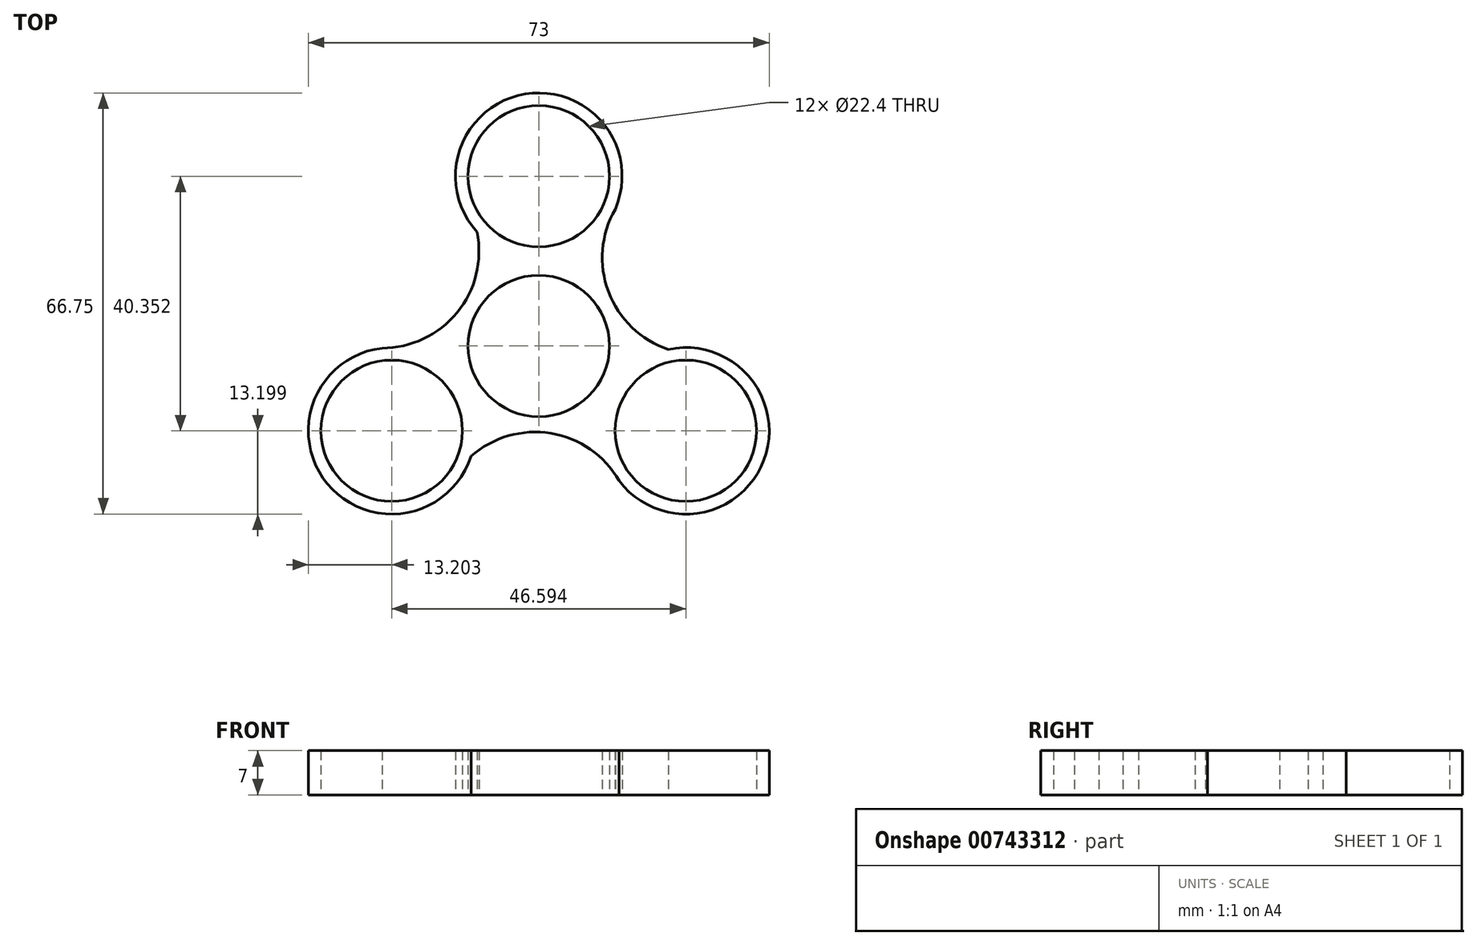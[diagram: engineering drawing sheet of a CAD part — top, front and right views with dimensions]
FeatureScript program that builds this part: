
annotation { "Feature Type Name" : "Feature", "Feature Type Description" : "" }
export const myFeature = defineFeature(function(context is Context, id is Id, definition is map)
    precondition{}
    {
        {
            var Q0;
            Q0=qCreatedBy(makeId("Top.planeOp"),FACE);
            var sketch = newSketch(context, id + "F0", { "sketchPlane" : qUnion([Q0])});
            skCircle(sketch, "E0", {"center": v(0, 0) * mm, "radius": 11.2 * mm});
            skCircle(sketch, "E1", {"center": v(0, 26.9) * mm, "radius": 11.2 * mm});
            skArc(sketch, "E2", {"start": v(11.36, 20.18) * mm, "mid": v(-1.33, 40.03) * mm, "end": v(-9.78, 18.03) * mm});
            skArc(sketch, "E3.1.0", {"start": v(-23.15, -0.25) * mm, "mid": v(-34, -21.17) * mm, "end": v(-10.73, -17.48) * mm});
            skCircle(sketch, "E3.1.1", {"center": v(-23.3, -13.45) * mm, "radius": 11.2 * mm});
            skArc(sketch, "E3.2.0", {"start": v(11.8, -19.93) * mm, "mid": v(35.34, -18.86) * mm, "end": v(20.5, -0.55) * mm});
            skCircle(sketch, "E3.2.1", {"center": v(23.3, -13.45) * mm, "radius": 11.2 * mm});
            skArc(sketch, "E4", {"start": v(12.13, 21.69) * mm, "mid": v(11.04, 8.58) * mm, "end": v(20.5, -0.55) * mm});
            skArc(sketch, "E5.1.0", {"start": v(-24.84, -0.34) * mm, "mid": v(-12.95, 5.27) * mm, "end": v(-9.78, 18.03) * mm});
            skArc(sketch, "E5.2.0", {"start": v(12.72, -21.34) * mm, "mid": v(1.91, -13.85) * mm, "end": v(-10.73, -17.48) * mm});
            skSolve(sketch);
        }
        {
            var Q0;
            Q0=makeQuery(id+"F0.imprint","IMPRINT",FACE,{"disambiguationData":[TD([[makeQuery(id+"F0.imprint","IMPRINT",EDGE,{"derivedFrom":sQuery(id+"F0.wireOp",EDGE,"E0")}),-1.0]])]});
            extrude(context, id + "F1", {"entities" : qUnion([Q0]), "depth" : 7 * mm, "offsetDistance" : 25 * mm});
        }
    });
